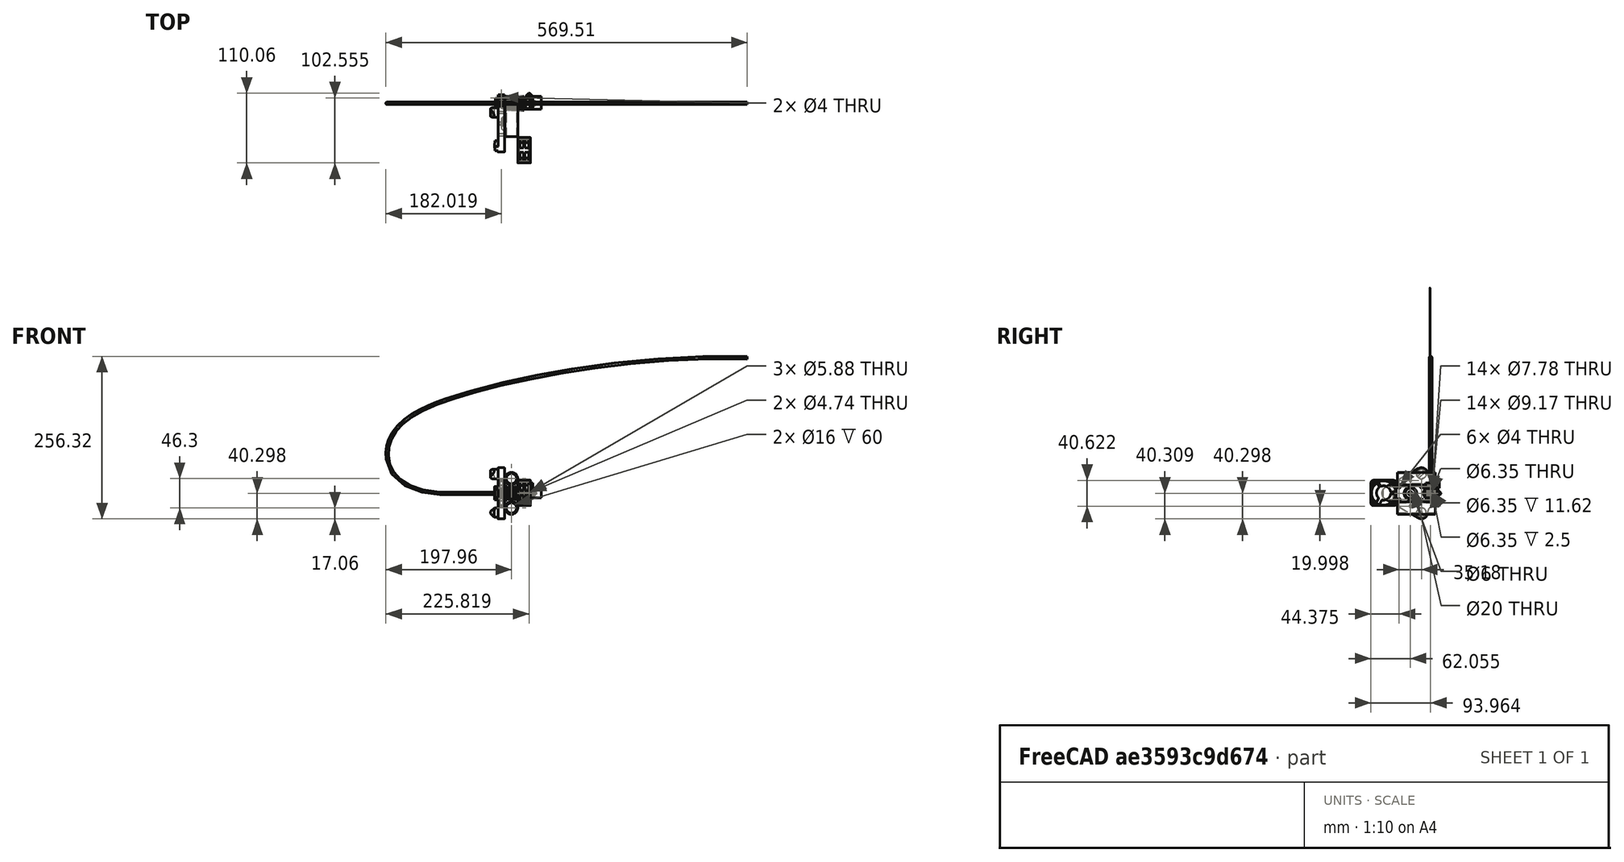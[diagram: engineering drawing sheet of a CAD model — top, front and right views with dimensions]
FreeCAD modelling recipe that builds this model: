
FCSTD DOCUMENT  (FreeCAD 0.20R29177 (Git))
Label: AT_932a_hotend_withfan
License: All rights reserved
LicenseURL: http://en.wikipedia.org/wiki/All_rights_reserved
objects: Part::FeaturePython×5, App::FeaturePython×2, PartDesign::ShapeBinder×2, Sketcher::SketchObject×2, PartDesign::AdditivePipe×1, PartDesign::Body×1
note: 12 computed .brp shape members not serialized (recipe doc carries the construction recipe); baked Part::Feature solids carry a one-line shape summary decoded from their .brp

FEATURE [Part::FeaturePython] b_AP_012a_toolHolder_GA3Dtech_001_  label="AP_012a_toolHolder_GA3Dtech_001"  # a2plus imported part (geometry in sourceFile) (typed FeaturePython)
  a2p_Version = V0.1
  fixedPosition = true
  objectType = a2pPart
  sourceFile = ./AP_012a_toolHolder_GA3Dtech.FCStd
  subassemblyImport = false
  timeLastImport = 1656487314
  updateColors = true
FEATURE [Part::FeaturePython] b_AT_hotend_horizontal_001_  label="AT_hotend_horizontal_001"  # a2plus imported part (geometry in sourceFile) (typed FeaturePython)
  Placement = pos=(-4.94089,57.1337,6.03789) rot=(0,-1,0;1.5708rad)
  a2p_Version = V0.1
  fixedPosition = false
  objectType = a2pPart
  sourceFile = ./AT_hotend_horizontal.FCStd
  subassemblyImport = false
  timeLastImport = 1656523934
  updateColors = true
FEATURE [App::FeaturePython] planeCoincident_001  label="planeCoincident_001__AP_012a_toolHolder_GA3Dtech_001"  # a2plus constraint (typed FeaturePython)
  Object1 = b_AT_hotend_horizontal_001_
  Object2 = b_AP_012a_toolHolder_GA3Dtech_001_
  ParentTreeObject = -> b_AT_hotend_horizontal_001_
  SubElement1 = Face92
  SubElement2 = Face3
  Suppressed = false
  Type = plane
  directionConstraint = 0
  offset = 0
FEATURE [App::FeaturePython] planeCoincident_001_mirror  label="planeCoincident_001__AT_hotend_horizontal_001"  # a2plus constraint (typed FeaturePython)
  Object1 = b_AT_hotend_horizontal_001_
  Object2 = b_AP_012a_toolHolder_GA3Dtech_001_
  ParentTreeObject = -> b_AP_012a_toolHolder_GA3Dtech_001_
  SubElement1 = Face92
  SubElement2 = Face3
  Suppressed = false
  Type = plane
  directionConstraint = 0
  offset = 0
FEATURE [PartDesign::ShapeBinder] ShapeBinder
  Placement = pos=(-4.94089,57.1337,6.03789) rot=(0,-1,0;1.5708rad)
  Support = -> [b_AT_hotend_horizontal_001_]
  TraceSupport = false
FEATURE [Sketcher::SketchObject] Sketch001
  FullyConstrained = false
  MapMode = 5
  Placement = pos=(-4.94089,57.1337,6.03789) rot=(0,-1,0;1.5708rad)
  Support = -> [ShapeBinder]
  sketch-geometry (2):
    g0: Circle CenterX=0 CenterY=-1e-06 CenterZ=0 NormalX=0 NormalY=0 NormalZ=1 AngleXU=0 Radius=2
    g1: Circle CenterX=0 CenterY=-1e-06 CenterZ=0 NormalX=0 NormalY=0 NormalZ=1 AngleXU=0 Radius=0.861519
  constraints (2):
    c: Diameter(g0) = 4
    c: Coincident(g1,g0)
FEATURE [PartDesign::ShapeBinder] ShapeBinder001
  Support = -> [b_AP_012a_toolHolder_GA3Dtech_001_]
  TraceSupport = false
FEATURE [Sketcher::SketchObject] Sketch
  FullyConstrained = false
  MapMode = 5
  Placement = pos=(0,70.725,0) rot=(0,0.707107,0.707107;3.14159rad)
  Support = -> [ShapeBinder001]
  sketch-geometry (12):
    g0: LineSegment StartX=4.79604 StartY=5.93311 StartZ=0 EndX=92.6904 EndY=5.93311 EndZ=0
    g1-g6: Circle x6 (B-spline internal-alignment scaffolding for g7; pole/knot coordinates omitted)
    g7: BSplineCurve PolesCount=6 KnotsCount=4 Degree=3 IsPeriodic=0
    g8-g11: GeomPoint x4 (B-spline internal-alignment scaffolding for g7; pole/knot coordinates omitted)
  constraints (6):
    c: Horizontal(g0)
    c: Weight(g1) = 1
    c: Coincident(g7,g0)
    c: Equal(g1, g2-g6) x5
    c: InternalAlignment(g1-g6 -> g7) x6
    c: InternalAlignment(g8-g11 -> g7) x4
FEATURE [PartDesign::AdditivePipe] AdditivePipe
  AuxilleryCurvelinear = true
  AuxillerySpineTangent = false
  Binormal = (0,0,0)
  Mode = 0
  Placement = pos=(-4.94089,57.1337,6.03789) rot=(0,-1,0;1.5708rad)
  Profile = -> Sketch001
  Spine = -> Sketch
  SpineTangent = false
  Transformation = 0
  Transition = 0
FEATURE [PartDesign::Body] Body
  Group = -> [ShapeBinder,Sketch001,ShapeBinder001,Sketch,AdditivePipe]
  Origin = -> Origin
  Tip = -> AdditivePipe
FEATURE [Part::FeaturePython] b_AT_achat_fan40x40x20_001_  label="AT_achat_fan40x40x20_001"  # a2plus imported part (geometry in sourceFile) (typed FeaturePython)
  Placement = pos=(50.3359,-16.834,6.52254) rot=(0,-1,0;1.5708rad)
  a2p_Version = V0.1
  fixedPosition = false
  objectType = a2pPart
  sourceFile = ./AT_achat_fan40x40x20.FCStd
  subassemblyImport = false
  timeLastImport = 1657441506
  updateColors = true
FEATURE [Part::FeaturePython] Tube  # WARN: FeaturePython — macro-defined, semantics opaque (R4)
  AttacherType = Attacher::AttachEngine3D
  Height = 60
  InnerRadius = 8
  OuterRadius = 10
  Placement = pos=(20.2,64.8,-17.2) rot=(1,0,0;1.5708rad)
FEATURE [Part::FeaturePython] Tube001  # WARN: FeaturePython — macro-defined, semantics opaque (R4)
  AttacherType = Attacher::AttachEngine3D
  Height = 60
  InnerRadius = 8
  OuterRadius = 10
  Placement = pos=(20.2,64.8,29.1) rot=(1,0,0;1.5708rad)
